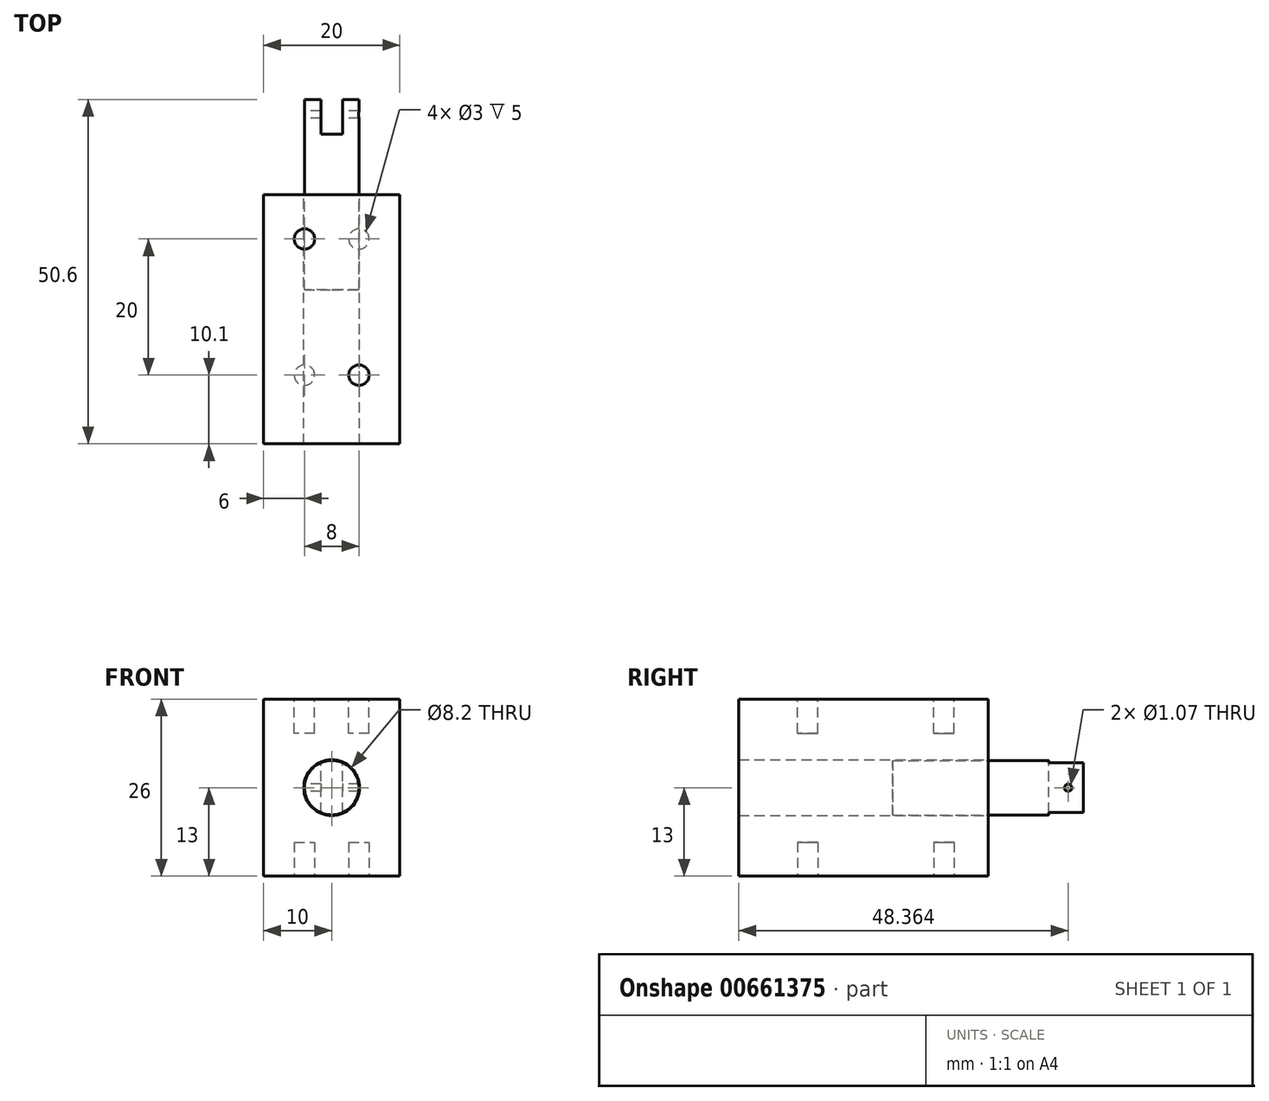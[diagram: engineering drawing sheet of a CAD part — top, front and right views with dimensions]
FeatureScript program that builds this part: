
annotation { "Feature Type Name" : "Feature", "Feature Type Description" : "" }
export const myFeature = defineFeature(function(context is Context, id is Id, definition is map)
    precondition{}
    {
        {
            var Q0;
            Q0=qCreatedBy(makeId("Front.planeOp"),FACE);
            var sketch = newSketch(context, id + "F0", { "sketchPlane" : qUnion([Q0])});
            skCircle(sketch, "E0", {"center": v(0, 0) * mm, "radius": 4.1 * mm});
            skLineSegment(sketch, "E1.bottom", {"start": v(10, -13) * mm, "end": v(-10, -13) * mm});
            skLineSegment(sketch, "E1.top", {"start": v(10, 13) * mm, "end": v(-10, 13) * mm});
            skLineSegment(sketch, "E1.left", {"start": v(10, -13) * mm, "end": v(10, 13) * mm});
            skLineSegment(sketch, "E1.right", {"start": v(-10, -13) * mm, "end": v(-10, 13) * mm});
            skCircle(sketch, "E2", {"center": v(0, 0) * mm, "radius": 4 * mm});
            skSolve(sketch);
        }
        {
            var Q0;
            Q0=makeQuery(id+"F0.imprint","IMPRINT",FACE,{"disambiguationData":[TD([[makeQuery(id+"F0.imprint","IMPRINT",EDGE,{"derivedFrom":sQuery(id+"F0.wireOp",EDGE,"E0")}),-1.0]])]});
            extrude(context, id + "F1", {"entities" : qUnion([Q0]), "depth" : 36.6 * mm, "offsetDistance" : 25 * mm});
        }
        {
            var Q0;
            Q0=makeQuery(id+"F0.imprint","IMPRINT",FACE,{"disambiguationData":[TD([[makeQuery(id+"F0.imprint","IMPRINT",EDGE,{"derivedFrom":sQuery(id+"F0.wireOp",EDGE,"E2")}),1.0]])]});
            extrude(context, id + "F2", {"entities" : qUnion([Q0]), "endBound" : BoundingType.SYMMETRIC, "depth" : 28 * mm, "offsetDistance" : 25 * mm});
        }
        {
            var Q0;
            Q0=makeQuery(id+"F1.opExtrude","SWEPT_FACE",FACE,{"disambiguationData":[OSD([sQuery(id+"F0.wireOp",EDGE,"E1.top")])]});
            var sketch = newSketch(context, id + "F3", { "sketchPlane" : qUnion([Q0])});
            skLineSegment(sketch, "E3.bottom", {"start": v(-10, 0) * mm, "end": v(10, 0) * mm, "construction": true});
            skLineSegment(sketch, "E3.top", {"start": v(-10, -5) * mm, "end": v(10, -5) * mm, "construction": true});
            skLineSegment(sketch, "E3.left", {"start": v(-10, 0) * mm, "end": v(-10, -5) * mm, "construction": true});
            skLineSegment(sketch, "E3.right", {"start": v(10, 0) * mm, "end": v(10, -5) * mm, "construction": true});
            skLineSegment(sketch, "E4.bottom", {"start": v(-10, 0) * mm, "end": v(-5.5, 0) * mm, "construction": true});
            skLineSegment(sketch, "E4.top", {"start": v(-10, -36.6) * mm, "end": v(-5.5, -36.6) * mm, "construction": true});
            skLineSegment(sketch, "E4.left", {"start": v(-10, 0) * mm, "end": v(-10, -36.6) * mm, "construction": true});
            skLineSegment(sketch, "E4.right", {"start": v(-5.5, 0) * mm, "end": v(-5.5, -36.6) * mm, "construction": true});
            skLineSegment(sketch, "E5.bottom", {"start": v(-5.5, -5) * mm, "end": v(5.5, -5) * mm, "construction": true});
            skLineSegment(sketch, "E5.top", {"start": v(-5.5, -28) * mm, "end": v(5.5, -28) * mm, "construction": true});
            skLineSegment(sketch, "E5.left", {"start": v(-5.5, -5) * mm, "end": v(-5.5, -28) * mm, "construction": true});
            skLineSegment(sketch, "E5.right", {"start": v(5.5, -5) * mm, "end": v(5.5, -28) * mm, "construction": true});
            skCircle(sketch, "E6", {"center": v(-4, -6.5) * mm, "radius": 1.5 * mm});
            skCircle(sketch, "E7", {"center": v(4, -26.5) * mm, "radius": 1.5 * mm});
            skSolve(sketch);
        }
        {
            var Q0;
            Q0=makeQuery(id+"F3.imprint","IMPRINT",FACE,{"disambiguationData":[TD([[makeQuery(id+"F3.imprint","IMPRINT",EDGE,{"derivedFrom":sQuery(id+"F3.wireOp",EDGE,"E6")}),1.0]])]});
            var Q1;
            Q1=makeQuery(id+"F3.imprint","IMPRINT",FACE,{"disambiguationData":[TD([[makeQuery(id+"F3.imprint","IMPRINT",EDGE,{"derivedFrom":sQuery(id+"F3.wireOp",EDGE,"E7")}),1.0]])]});
            extrude(context, id + "F4", {"entities" : qUnion([Q0, Q1]), "operationType" : NewBodyOperationType.REMOVE, "oppositeDirection" : true, "depth" : 5 * mm, "offsetDistance" : 25 * mm});
        }
        {
            var Q0;
            Q0=makeQuery(id+"F1.opExtrude","SWEPT_FACE",FACE,{"disambiguationData":[OSD([sQuery(id+"F0.wireOp",EDGE,"E1.bottom")])]});
            var sketch = newSketch(context, id + "F5", { "sketchPlane" : qUnion([Q0])});
            skLineSegment(sketch, "E8.bottom", {"start": v(10, 0) * mm, "end": v(-10, 0) * mm, "construction": true});
            skLineSegment(sketch, "E8.top", {"start": v(10, 5) * mm, "end": v(-10, 5) * mm, "construction": true});
            skLineSegment(sketch, "E8.left", {"start": v(10, 0) * mm, "end": v(10, 5) * mm, "construction": true});
            skLineSegment(sketch, "E8.right", {"start": v(-10, 0) * mm, "end": v(-10, 5) * mm, "construction": true});
            skLineSegment(sketch, "E9.bottom", {"start": v(10, 0) * mm, "end": v(5.5, 0) * mm, "construction": true});
            skLineSegment(sketch, "E9.top", {"start": v(10, 36.6) * mm, "end": v(5.5, 36.6) * mm, "construction": true});
            skLineSegment(sketch, "E9.left", {"start": v(10, 0) * mm, "end": v(10, 36.6) * mm, "construction": true});
            skLineSegment(sketch, "E9.right", {"start": v(5.5, 0) * mm, "end": v(5.5, 36.6) * mm, "construction": true});
            skLineSegment(sketch, "E10.bottom", {"start": v(5.5, 5) * mm, "end": v(-5.5, 5) * mm, "construction": true});
            skLineSegment(sketch, "E10.top", {"start": v(5.5, 28) * mm, "end": v(-5.5, 28) * mm, "construction": true});
            skLineSegment(sketch, "E10.left", {"start": v(5.5, 5) * mm, "end": v(5.5, 28) * mm, "construction": true});
            skLineSegment(sketch, "E10.right", {"start": v(-5.5, 5) * mm, "end": v(-5.5, 28) * mm, "construction": true});
            skCircle(sketch, "E11", {"center": v(4, 6.5) * mm, "radius": 1.5 * mm});
            skCircle(sketch, "E12", {"center": v(-4, 26.5) * mm, "radius": 1.5 * mm});
            skSolve(sketch);
        }
        {
            var Q0;
            Q0=makeQuery(id+"F5.imprint","IMPRINT",FACE,{"disambiguationData":[TD([[makeQuery(id+"F5.imprint","IMPRINT",EDGE,{"derivedFrom":sQuery(id+"F5.wireOp",EDGE,"E12")}),1.0]])]});
            var Q1;
            Q1=makeQuery(id+"F5.imprint","IMPRINT",FACE,{"disambiguationData":[TD([[makeQuery(id+"F5.imprint","IMPRINT",EDGE,{"derivedFrom":sQuery(id+"F5.wireOp",EDGE,"E11")}),1.0]])]});
            extrude(context, id + "F6", {"entities" : qUnion([Q0, Q1]), "operationType" : NewBodyOperationType.REMOVE, "oppositeDirection" : true, "depth" : 5 * mm, "offsetDistance" : 25 * mm});
        }
        {
            var Q0;
            Q0=makeQuery(id+"F2.opExtrude","CAP_FACE",FACE,{"disambiguationData":[OSD([sQuery(id+"F0.wireOp",EDGE,"E2")])],"isStart":true});
            var sketch = newSketch(context, id + "F7", { "sketchPlane" : qUnion([Q0])});
            skLineSegment(sketch, "E13.bottom", {"start": v(-1.6, -5) * mm, "end": v(1.6, -5) * mm});
            skLineSegment(sketch, "E13.top", {"start": v(-1.6, 5) * mm, "end": v(1.6, 5) * mm});
            skLineSegment(sketch, "E13.left", {"start": v(-1.6, -5) * mm, "end": v(-1.6, 5) * mm});
            skLineSegment(sketch, "E13.right", {"start": v(1.6, -5) * mm, "end": v(1.6, 5) * mm});
            skPoint(sketch, "E13.middle", {"position": v(0, 0) * mm});
            skSolve(sketch);
        }
        {
            var Q0;
            {var subQ0=sQuery(id+"F7.wireOp",EDGE,"E13.top");Q0=makeQuery(id+"F7.imprint","IMPRINT",FACE,{"disambiguationData":[TD([[makeQuery(id+"F7.imprint","IMPRINT",EDGE,{"derivedFrom":subQ0}),-1.0]])]});}
            var Q1;
            {var subQ0=sQuery(id+"F7.wireOp",EDGE,"E13.left");var subQ1=makeQuery(id+"F2.opExtrude","CAP_EDGE",EDGE,{"disambiguationData":[OSD([sQuery(id+"F0.wireOp",EDGE,"E2")])],"isStart":true});var subQ2=makeQuery(id+"F7.imprint","INTERSECT",VERTEX,{"disambiguationData":[OD(0.0)],"derivedFrom":[subQ1,subQ0]});Q1=makeQuery(id+"F7.imprint","IMPRINT",FACE,{"disambiguationData":[TD([[makeQuery(id+"F7.imprint","IMPRINT",EDGE,{"disambiguationData":[TD([[subQ2,-1.0]])],"derivedFrom":subQ0}),-1.0]])]});}
            var Q2;
            {var subQ0=sQuery(id+"F7.wireOp",EDGE,"E13.bottom");Q2=makeQuery(id+"F7.imprint","IMPRINT",FACE,{"disambiguationData":[TD([[makeQuery(id+"F7.imprint","IMPRINT",EDGE,{"derivedFrom":subQ0}),1.0]])]});}
            extrude(context, id + "F8", {"entities" : qUnion([Q0, Q1, Q2]), "operationType" : NewBodyOperationType.REMOVE, "oppositeDirection" : true, "depth" : 5.1 * mm, "offsetDistance" : 25 * mm});
        }
        {
            var Q0;
            Q0=makeQuery(id+"F8.boolean.opBoolean","COPY",FACE,{"derivedFrom":makeQuery(id+"F8.opExtrude","SWEPT_FACE",FACE,{"disambiguationData":[OSD([sQuery(id+"F7.wireOp",EDGE,"E13.left")])]})});
            var sketch = newSketch(context, id + "F9", { "sketchPlane" : qUnion([Q0])});
            skLineSegment(sketch, "E14.bottom", {"start": v(-14, 3.67) * mm, "end": v(-8.9, 3.67) * mm, "construction": true});
            skLineSegment(sketch, "E14.top", {"start": v(-14, -3.67) * mm, "end": v(-8.9, -3.67) * mm, "construction": true});
            skLineSegment(sketch, "E14.left", {"start": v(-14, 3.67) * mm, "end": v(-14, -3.67) * mm, "construction": true});
            skLineSegment(sketch, "E14.right", {"start": v(-8.9, 3.67) * mm, "end": v(-8.9, -3.67) * mm, "construction": true});
            skLineSegment(sketch, "E15.bottom", {"start": v(-14, 3.67) * mm, "end": v(-12.3, 3.67) * mm, "construction": true});
            skLineSegment(sketch, "E15.top", {"start": v(-14, -3.67) * mm, "end": v(-12.3, -3.67) * mm, "construction": true});
            skLineSegment(sketch, "E15.right", {"start": v(-12.3, 3.67) * mm, "end": v(-12.3, -3.67) * mm, "construction": true});
            skCircle(sketch, "E16", {"center": v(-11.76, 0) * mm, "radius": 0.54 * mm});
            skSolve(sketch);
        }
        {
            var Q0;
            Q0=makeQuery(id+"F9.imprint","IMPRINT",FACE,{"disambiguationData":[TD([[makeQuery(id+"F9.imprint","IMPRINT",EDGE,{"derivedFrom":sQuery(id+"F9.wireOp",EDGE,"E16")}),1.0]])]});
            extrude(context, id + "F10", {"entities" : qUnion([Q0]), "operationType" : NewBodyOperationType.REMOVE, "endBound" : BoundingType.SYMMETRIC, "oppositeDirection" : true, "depth" : 25 * mm, "offsetDistance" : 25 * mm});
        }
    });
